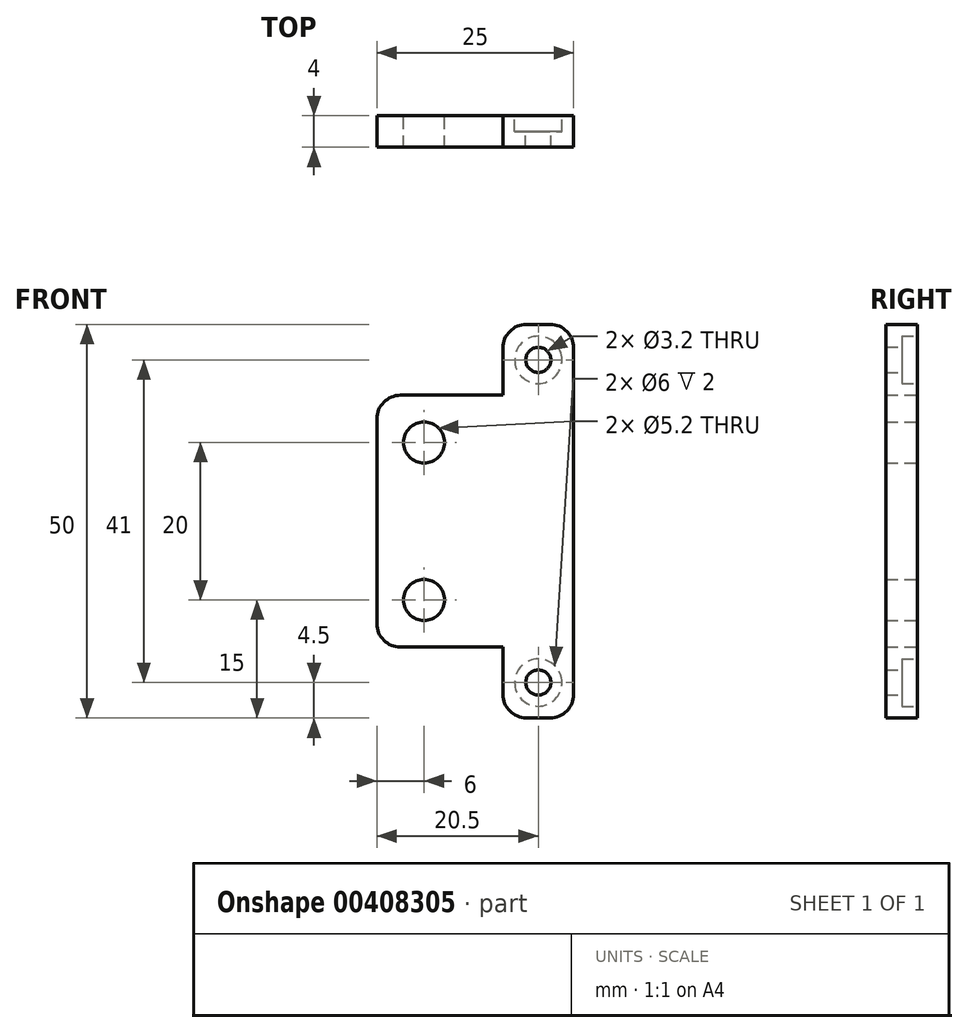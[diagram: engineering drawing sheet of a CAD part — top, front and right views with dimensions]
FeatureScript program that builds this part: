
annotation { "Feature Type Name" : "Feature", "Feature Type Description" : "" }
export const myFeature = defineFeature(function(context is Context, id is Id, definition is map)
    precondition{}
    {
        {
            var Q0;
            Q0=qCreatedBy(makeId("Front.planeOp"),FACE);
            var sketch = newSketch(context, id + "F0", { "sketchPlane" : qUnion([Q0])});
            skLineSegment(sketch, "E0.bottom", {"start": v(0, 0) * mm, "end": v(210, 0) * mm, "construction": true});
            skLineSegment(sketch, "E0.top", {"start": v(0, -50) * mm, "end": v(210, -50) * mm, "construction": true});
            skLineSegment(sketch, "E0.left", {"start": v(0, 0) * mm, "end": v(0, -50) * mm, "construction": true});
            skLineSegment(sketch, "E0.right", {"start": v(210, 0) * mm, "end": v(210, -50) * mm, "construction": true});
            skPoint(sketch, "E1", {"position": v(105, 0) * mm});
            skPoint(sketch, "E2", {"position": v(0, -25) * mm});
            skLineSegment(sketch, "E3", {"start": v(105, 0) * mm, "end": v(105, -50) * mm, "construction": true});
            skLineSegment(sketch, "E4", {"start": v(0, -25) * mm, "end": v(210, -25) * mm, "construction": true});
            skPoint(sketch, "E5", {"position": v(4.5, -4.5) * mm});
            skPoint(sketch, "E6.MirrorP", {"position": v(4.5, -45.5) * mm});
            skPoint(sketch, "E7.MirrorP", {"position": v(205.5, -4.5) * mm});
            skPoint(sketch, "E8.MirrorP", {"position": v(205.5, -45.5) * mm});
            skPoint(sketch, "E9", {"position": v(-10, -15) * mm});
            skPoint(sketch, "E10.MirrorP", {"position": v(-10, -35) * mm});
            skLineSegment(sketch, "E11", {"start": v(-16, -9) * mm, "end": v(-16, -41) * mm});
            skPoint(sketch, "E12", {"position": v(-16, -25) * mm});
            skLineSegment(sketch, "E13", {"start": v(-16, -9) * mm, "end": v(0, -9) * mm});
            skLineSegment(sketch, "E14", {"start": v(-16, -41) * mm, "end": v(0, -41) * mm});
            skLineSegment(sketch, "E15", {"start": v(0, -9) * mm, "end": v(0, 0) * mm});
            skLineSegment(sketch, "E16", {"start": v(0, 0) * mm, "end": v(9, 0) * mm});
            skLineSegment(sketch, "E17.MirrorCS", {"start": v(0, -41) * mm, "end": v(0, -50) * mm});
            skLineSegment(sketch, "E18.MirrorCS", {"start": v(0, -50) * mm, "end": v(9, -50) * mm});
            skLineSegment(sketch, "E19", {"start": v(9, -50) * mm, "end": v(9, 0) * mm});
            skLineSegment(sketch, "E20", {"start": v(0, -9) * mm, "end": v(0, -6) * mm});
            skLineSegment(sketch, "E21", {"start": v(0, -44) * mm, "end": v(0, -41) * mm});
            skSolve(sketch);
        }
        {
            var Q0;
            Q0=makeQuery(id+"F0.imprint","IMPRINT",FACE,{"disambiguationData":[TD([[makeQuery(id+"F0.imprint","IMPRINT",EDGE,{"derivedFrom":sQuery(id+"F0.wireOp",EDGE,"E11")}),1.0]])]});
            var Q1;
            Q1=makeQuery(id+"F0.imprint","IMPRINT",FACE,{"disambiguationData":[TD([[makeQuery(id+"F0.imprint","IMPRINT",EDGE,{"derivedFrom":sQuery(id+"F0.wireOp",EDGE,"E17.MirrorCS")}),1.0]])]});
            var Q2;
            Q2=makeQuery(id+"F0.imprint","IMPRINT",FACE,{"disambiguationData":[TD([[makeQuery(id+"F0.imprint","IMPRINT",EDGE,{"derivedFrom":sQuery(id+"F0.wireOp",EDGE,"E15")}),-1.0]])]});
            extrude(context, id + "F1", {"entities" : qUnion([Q0, Q1, Q2]), "depth" : 4 * mm});
        }
        {
            var Q0;
            Q0=sQuery(id+"F0.wireOp",VERTEX,"E5");
            var Q1;
            Q1=sQuery(id+"F0.wireOp",VERTEX,"E6.MirrorP");
            var Q2;
            Q2=makeQuery(id+"F1.opExtrude","SWEPT_BODY",BODY,{"disambiguationData":[OSD([sQuery(id+"F0.wireOp",EDGE,"E11"),sQuery(id+"F0.wireOp",EDGE,"E13"),sQuery(id+"F0.wireOp",EDGE,"E14"),sQuery(id+"F0.wireOp",EDGE,"E15"),sQuery(id+"F0.wireOp",EDGE,"E16"),sQuery(id+"F0.wireOp",EDGE,"E17.MirrorCS"),sQuery(id+"F0.wireOp",EDGE,"E18.MirrorCS"),sQuery(id+"F0.wireOp",EDGE,"E19")])]});
            hole(context, id + "F2", {"style" : HoleStyle.C_BORE, "endStyle" : HoleEndStyle.THROUGH, "oppositeDirection" : true, "holeDiameter" : 3.2 * mm, "cBoreDiameter" : 6 * mm, "cBoreDepth" : 2 * mm, "tappedDepth" : 12 * mm, "tapClearance" : 3, "locations" : qUnion([Q0, Q1]), "scope" : qUnion([Q2])});
        }
        {
            var Q0;
            Q0=sQuery(id+"F0.wireOp",VERTEX,"E9");
            var Q1;
            Q1=sQuery(id+"F0.wireOp",VERTEX,"E10.MirrorP");
            var Q2;
            Q2=makeQuery(id+"F1.opExtrude","SWEPT_BODY",BODY,{"disambiguationData":[OSD([sQuery(id+"F0.wireOp",EDGE,"E11"),sQuery(id+"F0.wireOp",EDGE,"E13"),sQuery(id+"F0.wireOp",EDGE,"E14"),sQuery(id+"F0.wireOp",EDGE,"E15"),sQuery(id+"F0.wireOp",EDGE,"E16"),sQuery(id+"F0.wireOp",EDGE,"E17.MirrorCS"),sQuery(id+"F0.wireOp",EDGE,"E18.MirrorCS"),sQuery(id+"F0.wireOp",EDGE,"E19")])]});
            hole(context, id + "F3", {"style" : HoleStyle.SIMPLE, "endStyle" : HoleEndStyle.THROUGH, "oppositeDirection" : true, "holeDiameter" : 5.2 * mm, "tappedDepth" : 12 * mm, "tapClearance" : 3, "locations" : qUnion([Q0, Q1]), "scope" : qUnion([Q2])});
        }
        {
            var Q0;
            Q0=makeQuery(id+"F1.opExtrude","SWEPT_EDGE",EDGE,{"disambiguationData":[OSD([sQuery(id+"F0.wireOp",EDGE,"E11"),sQuery(id+"F0.wireOp",EDGE,"E13")])]});
            var Q1;
            Q1=makeQuery(id+"F1.opExtrude","SWEPT_EDGE",EDGE,{"disambiguationData":[OSD([sQuery(id+"F0.wireOp",EDGE,"E11"),sQuery(id+"F0.wireOp",EDGE,"E14")])]});
            var Q2;
            Q2=makeQuery(id+"F1.opExtrude","SWEPT_EDGE",EDGE,{"disambiguationData":[OSD([sQuery(id+"F0.wireOp",EDGE,"E16"),sQuery(id+"F0.wireOp",EDGE,"E19")])]});
            var Q3;
            Q3=makeQuery(id+"F1.opExtrude","SWEPT_EDGE",EDGE,{"disambiguationData":[OSD([sQuery(id+"F0.wireOp",EDGE,"E15"),sQuery(id+"F0.wireOp",EDGE,"E16")])]});
            var Q4;
            Q4=makeQuery(id+"F1.opExtrude","SWEPT_EDGE",EDGE,{"disambiguationData":[OSD([sQuery(id+"F0.wireOp",EDGE,"E17.MirrorCS"),sQuery(id+"F0.wireOp",EDGE,"E18.MirrorCS")])]});
            var Q5;
            Q5=makeQuery(id+"F1.opExtrude","SWEPT_EDGE",EDGE,{"disambiguationData":[OSD([sQuery(id+"F0.wireOp",EDGE,"E18.MirrorCS"),sQuery(id+"F0.wireOp",EDGE,"E19")])]});
            fillet(context, id + "F4", {"entities" : qUnion([Q0, Q1, Q2, Q3, Q4, Q5]), "radius" : 3 * mm, "tangentPropagation" : true, "allowEdgeOverflow" : false});
        }
    });
